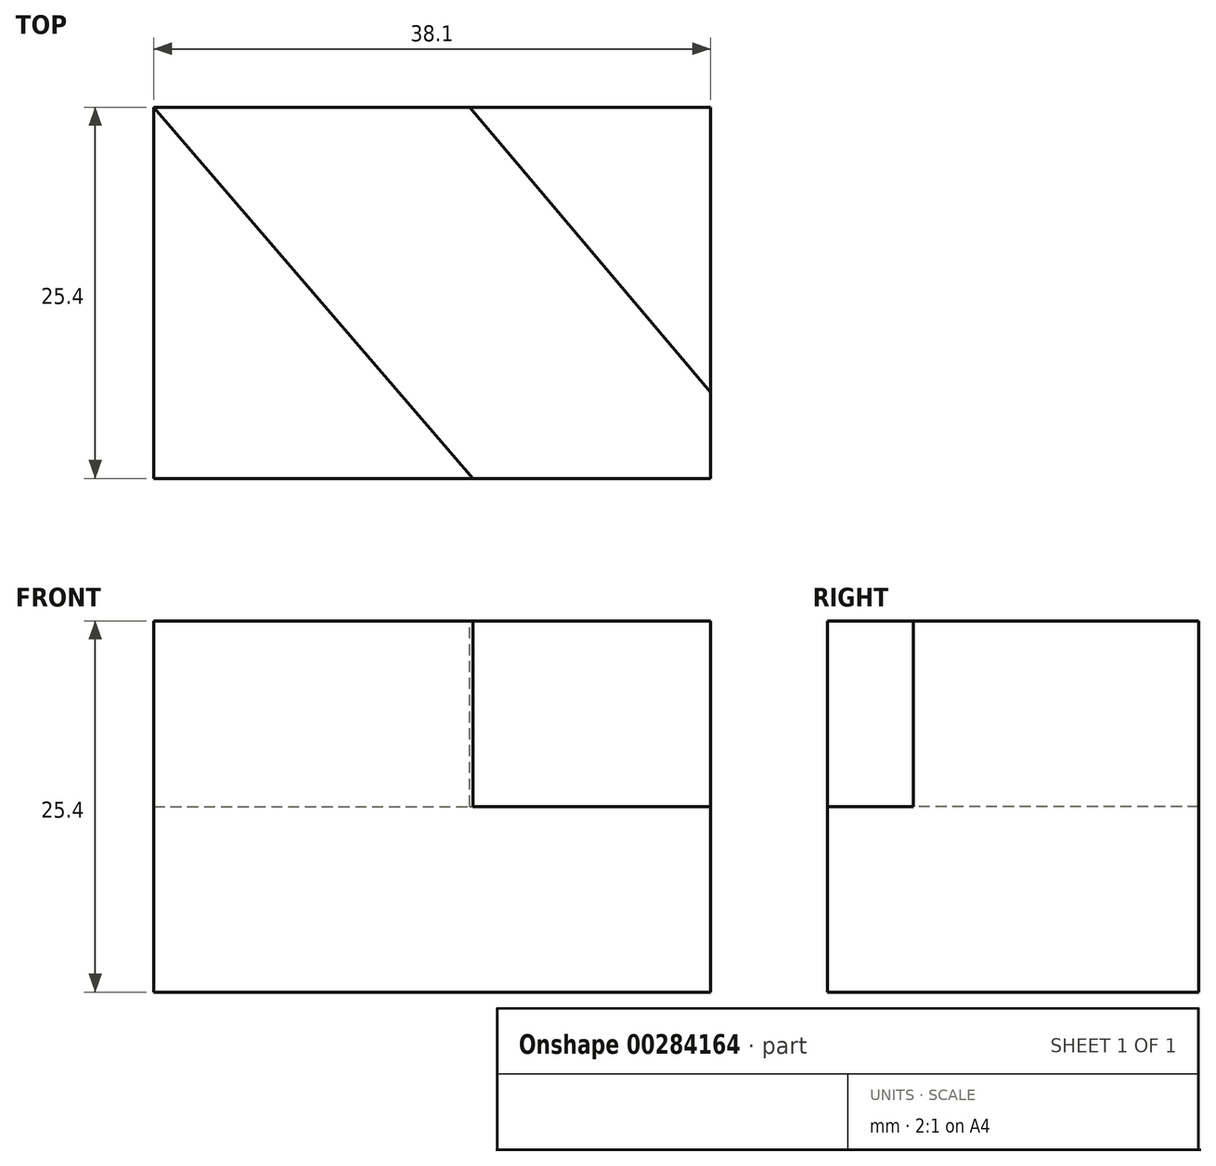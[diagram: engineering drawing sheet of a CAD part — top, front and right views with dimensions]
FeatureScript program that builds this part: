
annotation { "Feature Type Name" : "Feature", "Feature Type Description" : "" }
export const myFeature = defineFeature(function(context is Context, id is Id, definition is map)
    precondition{}
    {
        {
            var Q0;
            Q0=qCreatedBy(makeId("Top.planeOp"),FACE);
            var sketch = newSketch(context, id + "F0", { "sketchPlane" : qUnion([Q0])});
            skLineSegment(sketch, "E0.bottom", {"start": v(0, 0) * mm, "end": v(38.1, 0) * mm});
            skLineSegment(sketch, "E0.top", {"start": v(0, 25.4) * mm, "end": v(38.1, 25.4) * mm});
            skLineSegment(sketch, "E0.left", {"start": v(0, 0) * mm, "end": v(0, 25.4) * mm});
            skLineSegment(sketch, "E0.right", {"start": v(38.1, 0) * mm, "end": v(38.1, 25.4) * mm});
            skSolve(sketch);
        }
        {
            var Q0;
            Q0 = qSketchRegion(id + "F0", true);
            extrude(context, id + "F1", {"entities" : qUnion([Q0]), "depth" : 25.4 * mm});
        }
        {
            var Q0;
            Q0=makeQuery(id+"F1.opExtrude","CAP_FACE",FACE,{"disambiguationData":[OSD([sQuery(id+"F0.wireOp",EDGE,"E0.bottom"),sQuery(id+"F0.wireOp",EDGE,"E0.top"),sQuery(id+"F0.wireOp",EDGE,"E0.left"),sQuery(id+"F0.wireOp",EDGE,"E0.right")])],"isStart":false});
            var sketch = newSketch(context, id + "F2", { "sketchPlane" : qUnion([Q0])});
            skLineSegment(sketch, "E1", {"start": v(0, 25.4) * mm, "end": v(23.13, -1.52) * mm});
            skLineSegment(sketch, "E2", {"start": v(21.61, 25.4) * mm, "end": v(38.1, 5.88) * mm});
            skSolve(sketch);
        }
        {
            var Q0;
            {var subQ5=sQuery(id+"F2.wireOp",EDGE,"E2");Q0=makeQuery(id+"F2.imprint","IMPRINT",FACE,{"disambiguationData":[TD([[makeQuery(id+"F2.imprint","IMPRINT",EDGE,{"derivedFrom":subQ5}),-1.0]])]});}
            extrude(context, id + "F3", {"entities" : qUnion([Q0]), "operationType" : NewBodyOperationType.REMOVE, "oppositeDirection" : true, "depth" : 12.7 * mm});
        }
    });
